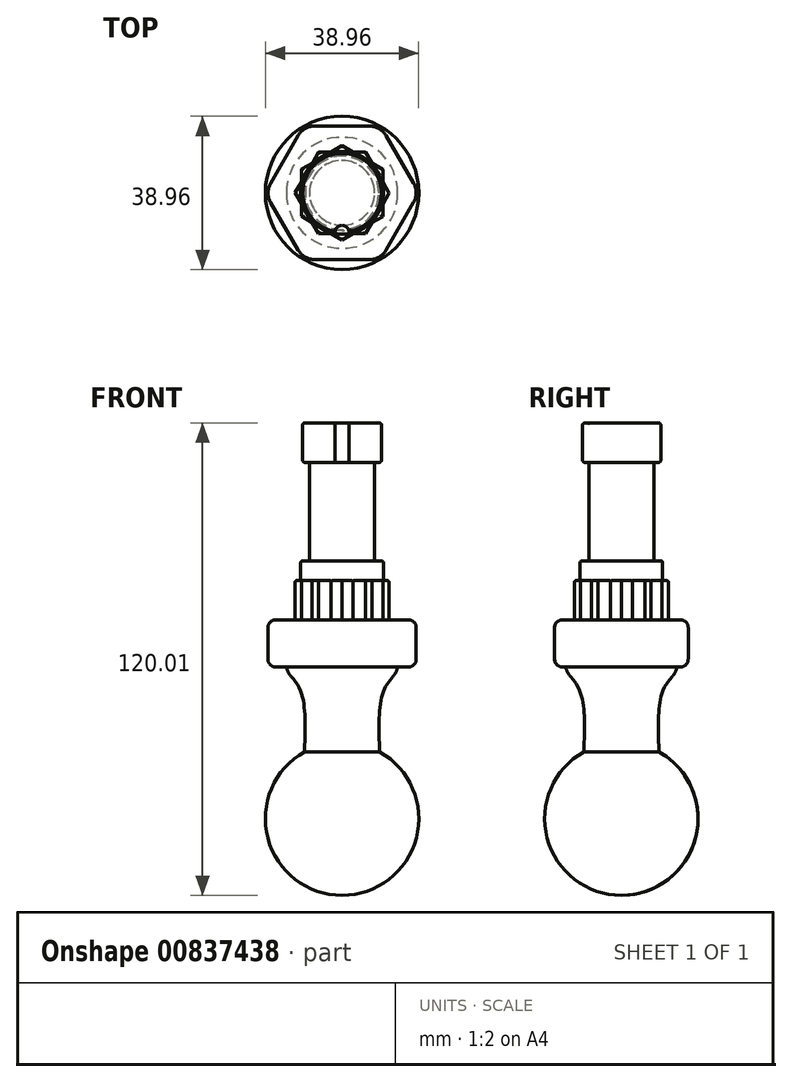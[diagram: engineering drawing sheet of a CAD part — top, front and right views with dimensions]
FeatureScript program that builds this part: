
annotation { "Feature Type Name" : "Feature", "Feature Type Description" : "" }
export const myFeature = defineFeature(function(context is Context, id is Id, definition is map)
    precondition{}
    {
        {
            var Q0;
            Q0=qCreatedBy(makeId("Top.planeOp"),FACE);
            var sketch = newSketch(context, id + "F0", { "sketchPlane" : qUnion([Q0])});
            skCircle(sketch, "E0.cCircle", {"center": v(0, 0) * mm, "radius": 11.95 * mm, "construction": true});
            skLineSegment(sketch, "E0.0", {"start": v(10.36, 5.96) * mm, "end": v(10.36, 2.75) * mm});
            skLineSegment(sketch, "E0.1", {"start": v(10.34, -6) * mm, "end": v(7.56, -7.6) * mm});
            skLineSegment(sketch, "E0.2", {"start": v(-0.02, -11.95) * mm, "end": v(-2.8, -10.34) * mm});
            skLineSegment(sketch, "E0.3", {"start": v(-10.36, -5.96) * mm, "end": v(-10.36, -2.75) * mm});
            skLineSegment(sketch, "E0.4", {"start": v(-10.34, 6) * mm, "end": v(-7.56, 7.6) * mm});
            skLineSegment(sketch, "E0.5", {"start": v(0.02, 11.95) * mm, "end": v(2.8, 10.34) * mm});
            skLineSegment(sketch, "E1", {"start": v(6, 10.34) * mm, "end": v(6.72, 11.59) * mm, "construction": true});
            skLineSegment(sketch, "E2.0", {"start": v(6, 10.34) * mm, "end": v(7.6, 7.56) * mm});
            skLineSegment(sketch, "E2.1", {"start": v(11.95, -0.02) * mm, "end": v(10.34, -2.8) * mm});
            skLineSegment(sketch, "E2.2", {"start": v(5.96, -10.36) * mm, "end": v(2.75, -10.36) * mm});
            skLineSegment(sketch, "E2.3", {"start": v(-6, -10.34) * mm, "end": v(-7.6, -7.56) * mm});
            skLineSegment(sketch, "E2.4", {"start": v(-11.95, 0.02) * mm, "end": v(-10.34, 2.8) * mm});
            skLineSegment(sketch, "E2.5", {"start": v(-5.96, 10.36) * mm, "end": v(-2.75, 10.36) * mm});
            skLineSegment(sketch, "E3.trimOffspring", {"start": v(-7.6, -7.56) * mm, "end": v(-10.36, -5.96) * mm});
            skPoint(sketch, "E4.orphan", {"position": v(-5.2, -8.95) * mm});
            skLineSegment(sketch, "E5.trimOffspring", {"start": v(-10.36, -2.75) * mm, "end": v(-11.95, 0.02) * mm});
            skLineSegment(sketch, "E6.trimOffspring", {"start": v(-2.8, -10.34) * mm, "end": v(-6, -10.34) * mm});
            skLineSegment(sketch, "E7.trimOffspring", {"start": v(2.75, -10.36) * mm, "end": v(-0.02, -11.95) * mm});
            skLineSegment(sketch, "E8.trimOffspring", {"start": v(7.56, -7.6) * mm, "end": v(5.96, -10.36) * mm});
            skLineSegment(sketch, "E9.trimOffspring", {"start": v(-10.34, 2.8) * mm, "end": v(-10.34, 6) * mm});
            skLineSegment(sketch, "E10.trimOffspring", {"start": v(-7.56, 7.6) * mm, "end": v(-5.96, 10.36) * mm});
            skLineSegment(sketch, "E11.trimOffspring", {"start": v(-2.75, 10.36) * mm, "end": v(0.02, 11.95) * mm});
            skLineSegment(sketch, "E12.trimOffspring", {"start": v(2.8, 10.34) * mm, "end": v(6, 10.34) * mm});
            skLineSegment(sketch, "E13.trimOffspring", {"start": v(7.6, 7.56) * mm, "end": v(10.36, 5.96) * mm});
            skPoint(sketch, "E14.orphan", {"position": v(5.2, 8.95) * mm});
            skLineSegment(sketch, "E15.trimOffspring", {"start": v(10.36, 2.75) * mm, "end": v(11.95, -0.02) * mm});
            skLineSegment(sketch, "E16.trimOffspring", {"start": v(10.34, -2.8) * mm, "end": v(10.34, -6) * mm});
            skSolve(sketch);
        }
        {
            var Q0;
            Q0=makeQuery(id+"F0.imprint","IMPRINT",FACE,{"disambiguationData":[TD([[makeQuery(id+"F0.imprint","IMPRINT",EDGE,{"derivedFrom":sQuery(id+"F0.wireOp",EDGE,"E0.0")}),-1.0]])]});
            extrude(context, id + "F1", {"entities" : qUnion([Q0]), "depth" : 10 * mm, "offsetDistance" : 25 * mm});
        }
        {
            var Q0;
            Q0=makeQuery(id+"F1.opExtrude","CAP_FACE",FACE,{"disambiguationData":[OSD([sQuery(id+"F0.wireOp",EDGE,"E0.0"),sQuery(id+"F0.wireOp",EDGE,"E0.1"),sQuery(id+"F0.wireOp",EDGE,"E0.2"),sQuery(id+"F0.wireOp",EDGE,"E0.3"),sQuery(id+"F0.wireOp",EDGE,"E0.4"),sQuery(id+"F0.wireOp",EDGE,"E0.5"),sQuery(id+"F0.wireOp",EDGE,"E2.0"),sQuery(id+"F0.wireOp",EDGE,"E2.1"),sQuery(id+"F0.wireOp",EDGE,"E2.2"),sQuery(id+"F0.wireOp",EDGE,"E2.3"),sQuery(id+"F0.wireOp",EDGE,"E2.4"),sQuery(id+"F0.wireOp",EDGE,"E2.5"),sQuery(id+"F0.wireOp",EDGE,"E3.trimOffspring"),sQuery(id+"F0.wireOp",EDGE,"E5.trimOffspring"),sQuery(id+"F0.wireOp",EDGE,"E6.trimOffspring"),sQuery(id+"F0.wireOp",EDGE,"E7.trimOffspring"),sQuery(id+"F0.wireOp",EDGE,"E8.trimOffspring"),sQuery(id+"F0.wireOp",EDGE,"E9.trimOffspring"),sQuery(id+"F0.wireOp",EDGE,"E10.trimOffspring"),sQuery(id+"F0.wireOp",EDGE,"E11.trimOffspring"),sQuery(id+"F0.wireOp",EDGE,"E12.trimOffspring"),sQuery(id+"F0.wireOp",EDGE,"E13.trimOffspring"),sQuery(id+"F0.wireOp",EDGE,"E15.trimOffspring"),sQuery(id+"F0.wireOp",EDGE,"E16.trimOffspring")])],"isStart":false});
            var sketch = newSketch(context, id + "F2", { "sketchPlane" : qUnion([Q0])});
            skLineSegment(sketch, "E17", {"start": v(-10.36, -2.75) * mm, "end": v(10.36, 2.75) * mm, "construction": true});
            skLineSegment(sketch, "E18", {"start": v(2.75, -10.36) * mm, "end": v(-2.75, 10.36) * mm, "construction": true});
            skCircle(sketch, "E19", {"center": v(0, 0) * mm, "radius": 10.5 * mm});
            skSolve(sketch);
        }
        {
            var Q0;
            Q0=makeQuery(id+"F2.imprint","IMPRINT",FACE,{"disambiguationData":[TD([[makeQuery(id+"F2.imprint","IMPRINT",EDGE,{"derivedFrom":sQuery(id+"F2.wireOp",EDGE,"E19")}),1.0]])]});
            extrude(context, id + "F3", {"entities" : qUnion([Q0]), "operationType" : NewBodyOperationType.ADD, "depth" : 5 * mm, "offsetDistance" : 25 * mm});
        }
        {
            var Q0;
            Q0=makeQuery(id+"F1.opExtrude","CAP_EDGE",EDGE,{"disambiguationData":[OSD([sQuery(id+"F0.wireOp",EDGE,"E2.5")])],"isStart":false});
            var Q1;
            Q1=makeQuery(id+"F1.opExtrude","CAP_EDGE",EDGE,{"disambiguationData":[OSD([sQuery(id+"F0.wireOp",EDGE,"E10.trimOffspring")])],"isStart":false});
            var Q2;
            Q2=makeQuery(id+"F1.opExtrude","CAP_EDGE",EDGE,{"disambiguationData":[OSD([sQuery(id+"F0.wireOp",EDGE,"E0.4")])],"isStart":false});
            var Q3;
            Q3=makeQuery(id+"F1.opExtrude","CAP_EDGE",EDGE,{"disambiguationData":[OSD([sQuery(id+"F0.wireOp",EDGE,"E9.trimOffspring")])],"isStart":false});
            var Q4;
            Q4=makeQuery(id+"F1.opExtrude","CAP_EDGE",EDGE,{"disambiguationData":[OSD([sQuery(id+"F0.wireOp",EDGE,"E2.4")])],"isStart":false});
            var Q5;
            Q5=makeQuery(id+"F1.opExtrude","CAP_EDGE",EDGE,{"disambiguationData":[OSD([sQuery(id+"F0.wireOp",EDGE,"E5.trimOffspring")])],"isStart":false});
            var Q6;
            Q6=makeQuery(id+"F1.opExtrude","CAP_EDGE",EDGE,{"disambiguationData":[OSD([sQuery(id+"F0.wireOp",EDGE,"E0.3")])],"isStart":false});
            var Q7;
            Q7=makeQuery(id+"F1.opExtrude","CAP_EDGE",EDGE,{"disambiguationData":[OSD([sQuery(id+"F0.wireOp",EDGE,"E3.trimOffspring")])],"isStart":false});
            var Q8;
            Q8=makeQuery(id+"F1.opExtrude","CAP_EDGE",EDGE,{"disambiguationData":[OSD([sQuery(id+"F0.wireOp",EDGE,"E2.3")])],"isStart":false});
            var Q9;
            Q9=makeQuery(id+"F1.opExtrude","CAP_EDGE",EDGE,{"disambiguationData":[OSD([sQuery(id+"F0.wireOp",EDGE,"E6.trimOffspring")])],"isStart":false});
            var Q10;
            Q10=makeQuery(id+"F1.opExtrude","CAP_EDGE",EDGE,{"disambiguationData":[OSD([sQuery(id+"F0.wireOp",EDGE,"E0.2")])],"isStart":false});
            var Q11;
            Q11=makeQuery(id+"F1.opExtrude","CAP_EDGE",EDGE,{"disambiguationData":[OSD([sQuery(id+"F0.wireOp",EDGE,"E7.trimOffspring")])],"isStart":false});
            var Q12;
            Q12=makeQuery(id+"F1.opExtrude","CAP_EDGE",EDGE,{"disambiguationData":[OSD([sQuery(id+"F0.wireOp",EDGE,"E2.2")])],"isStart":false});
            var Q13;
            Q13=makeQuery(id+"F1.opExtrude","CAP_EDGE",EDGE,{"disambiguationData":[OSD([sQuery(id+"F0.wireOp",EDGE,"E8.trimOffspring")])],"isStart":false});
            var Q14;
            Q14=makeQuery(id+"F1.opExtrude","CAP_EDGE",EDGE,{"disambiguationData":[OSD([sQuery(id+"F0.wireOp",EDGE,"E0.1")])],"isStart":false});
            var Q15;
            Q15=makeQuery(id+"F1.opExtrude","CAP_EDGE",EDGE,{"disambiguationData":[OSD([sQuery(id+"F0.wireOp",EDGE,"E16.trimOffspring")])],"isStart":false});
            var Q16;
            Q16=makeQuery(id+"F1.opExtrude","CAP_EDGE",EDGE,{"disambiguationData":[OSD([sQuery(id+"F0.wireOp",EDGE,"E2.1")])],"isStart":false});
            var Q17;
            Q17=makeQuery(id+"F1.opExtrude","CAP_EDGE",EDGE,{"disambiguationData":[OSD([sQuery(id+"F0.wireOp",EDGE,"E15.trimOffspring")])],"isStart":false});
            var Q18;
            Q18=makeQuery(id+"F1.opExtrude","CAP_EDGE",EDGE,{"disambiguationData":[OSD([sQuery(id+"F0.wireOp",EDGE,"E0.0")])],"isStart":false});
            var Q19;
            Q19=makeQuery(id+"F1.opExtrude","CAP_EDGE",EDGE,{"disambiguationData":[OSD([sQuery(id+"F0.wireOp",EDGE,"E13.trimOffspring")])],"isStart":false});
            var Q20;
            Q20=makeQuery(id+"F1.opExtrude","CAP_EDGE",EDGE,{"disambiguationData":[OSD([sQuery(id+"F0.wireOp",EDGE,"E2.0")])],"isStart":false});
            var Q21;
            Q21=makeQuery(id+"F1.opExtrude","CAP_EDGE",EDGE,{"disambiguationData":[OSD([sQuery(id+"F0.wireOp",EDGE,"E12.trimOffspring")])],"isStart":false});
            var Q22;
            Q22=makeQuery(id+"F1.opExtrude","CAP_EDGE",EDGE,{"disambiguationData":[OSD([sQuery(id+"F0.wireOp",EDGE,"E0.5")])],"isStart":false});
            var Q23;
            Q23=makeQuery(id+"F1.opExtrude","CAP_EDGE",EDGE,{"disambiguationData":[OSD([sQuery(id+"F0.wireOp",EDGE,"E11.trimOffspring")])],"isStart":false});
            fillet(context, id + "F4", {"entities" : qUnion([Q0, Q1, Q2, Q3, Q4, Q5, Q6, Q7, Q8, Q9, Q10, Q11, Q12, Q13, Q14, Q15, Q16, Q17, Q18, Q19, Q20, Q21, Q22, Q23]), "radius" : .5 * mm, "tangentPropagation" : true, "allowEdgeOverflow" : false});
        }
        {
            var Q0;
            Q0=makeQuery(id+"F3.opExtrude","CAP_FACE",FACE,{"disambiguationData":[OSD([sQuery(id+"F2.wireOp",EDGE,"E19")])],"isStart":false});
            var sketch = newSketch(context, id + "F5", { "sketchPlane" : qUnion([Q0])});
            skCircle(sketch, "E20", {"center": v(0, 0) * mm, "radius": 8.25 * mm});
            skSolve(sketch);
        }
        {
            var Q0;
            Q0=makeQuery(id+"F5.imprint","IMPRINT",FACE,{"disambiguationData":[TD([[makeQuery(id+"F5.imprint","IMPRINT",EDGE,{"derivedFrom":sQuery(id+"F5.wireOp",EDGE,"E20")}),1.0]])]});
            extrude(context, id + "F6", {"entities" : qUnion([Q0]), "operationType" : NewBodyOperationType.ADD, "depth" : 25 * mm, "offsetDistance" : 25 * mm});
        }
        {
            var Q0;
            Q0=makeQuery(id+"F6.opExtrude","CAP_FACE",FACE,{"disambiguationData":[OSD([sQuery(id+"F5.wireOp",EDGE,"E20")])],"isStart":false});
            var sketch = newSketch(context, id + "F7", { "sketchPlane" : qUnion([Q0])});
            skCircle(sketch, "E21", {"center": v(0, 0) * mm, "radius": 10 * mm});
            skSolve(sketch);
        }
        {
            var Q0;
            Q0=makeQuery(id+"F7.imprint","IMPRINT",FACE,{"disambiguationData":[TD([[makeQuery(id+"F7.imprint","IMPRINT",EDGE,{"derivedFrom":sQuery(id+"F7.wireOp",EDGE,"E21")}),1.0]])]});
            var Q1;
            Q1=makeQuery(id+"F7.imprint","IMPRINT",FACE,{"disambiguationData":[TD([[makeQuery(id+"F7.imprint","IMPRINT",EDGE,{"derivedFrom":makeQuery(id+"F6.opExtrude","CAP_EDGE",EDGE,{"disambiguationData":[OSD([sQuery(id+"F5.wireOp",EDGE,"E20")])],"isStart":false})}),1.0]])]});
            extrude(context, id + "F8", {"entities" : qUnion([Q0, Q1]), "operationType" : NewBodyOperationType.ADD, "depth" : 10 * mm, "offsetDistance" : 25 * mm});
        }
        {
            var Q0;
            Q0=makeQuery(id+"F8.opExtrude","CAP_FACE",FACE,{"disambiguationData":[OSD([sQuery(id+"F7.wireOp",EDGE,"E21")])],"isStart":true});
            var sketch = newSketch(context, id + "F9", { "sketchPlane" : qUnion([Q0])});
            skLineSegment(sketch, "E22", {"start": v(0, 10) * mm, "end": v(0, 8.25) * mm, "construction": true});
            skArc(sketch, "E23", {"start": v(0, 8.25) * mm, "mid": v(1.18, 8.7) * mm, "end": v(1.74, 9.85) * mm});
            skArc(sketch, "E24", {"start": v(0, 8.25) * mm, "mid": v(-1.18, 8.7) * mm, "end": v(-1.74, 9.85) * mm});
            skSolve(sketch);
        }
        {
            var Q0;
            {var subQ0=sQuery(id+"F9.wireOp",EDGE,"E23");Q0=makeQuery(id+"F9.imprint","IMPRINT",FACE,{"disambiguationData":[TD([[makeQuery(id+"F9.imprint","IMPRINT",EDGE,{"derivedFrom":subQ0}),1.0]])]});}
            extrude(context, id + "F10", {"entities" : qUnion([Q0]), "operationType" : NewBodyOperationType.REMOVE, "oppositeDirection" : true, "depth" : 25 * mm, "offsetDistance" : 25 * mm});
        }
        {
            var Q0;
            Q0=makeQuery(id+"F8.opExtrude","CAP_EDGE",EDGE,{"disambiguationData":[OSD([sQuery(id+"F7.wireOp",EDGE,"E21")])],"isStart":false});
            var Q1;
            Q1=makeQuery(id+"F10.boolean.opBoolean","INTERSECT",EDGE,{"derivedFrom":[makeQuery(id+"F8.opExtrude","CAP_FACE",FACE,{"disambiguationData":[OSD([sQuery(id+"F7.wireOp",EDGE,"E21")])],"isStart":false}),makeQuery(id+"F10.opExtrude","SWEPT_FACE",FACE,{"disambiguationData":[OSD([sQuery(id+"F9.wireOp",EDGE,"E23"),sQuery(id+"F9.wireOp",EDGE,"E24")])]})]});
            var Q2;
            Q2=makeQuery(id+"F10.boolean.opBoolean","COPY",EDGE,{"derivedFrom":makeQuery(id+"F10.opExtrude","SWEPT_EDGE",EDGE,{"disambiguationData":[OSD([sQuery(id+"F7.wireOp",EDGE,"E21"),sQuery(id+"F9.wireOp",EDGE,"E24")])]})});
            var Q3;
            Q3=makeQuery(id+"F10.boolean.opBoolean","COPY",EDGE,{"derivedFrom":makeQuery(id+"F10.opExtrude","SWEPT_EDGE",EDGE,{"disambiguationData":[OSD([sQuery(id+"F7.wireOp",EDGE,"E21"),sQuery(id+"F9.wireOp",EDGE,"E23")])]})});
            var Q4;
            Q4=makeQuery(id+"F8.opExtrude","CAP_EDGE",EDGE,{"disambiguationData":[OSD([sQuery(id+"F7.wireOp",EDGE,"E21")])],"isStart":true});
            var Q5;
            Q5=makeQuery(id+"F10.boolean.opBoolean","COPY",EDGE,{"disambiguationData":[OD(1.0)],"derivedFrom":makeQuery(id+"F10.opExtrude","CAP_EDGE",EDGE,{"disambiguationData":[OSD([sQuery(id+"F9.wireOp",EDGE,"E23"),sQuery(id+"F9.wireOp",EDGE,"E24")])],"isStart":true})});
            var Q6;
            Q6=makeQuery(id+"F10.boolean.opBoolean","COPY",EDGE,{"disambiguationData":[OD(0.0)],"derivedFrom":makeQuery(id+"F10.opExtrude","CAP_EDGE",EDGE,{"disambiguationData":[OSD([sQuery(id+"F9.wireOp",EDGE,"E23"),sQuery(id+"F9.wireOp",EDGE,"E24")])],"isStart":true})});
            fillet(context, id + "F11", {"entities" : qUnion([Q0, Q1, Q2, Q3, Q4, Q5, Q6]), "radius" : .5 * mm, "tangentPropagation" : true, "allowEdgeOverflow" : false});
        }
        {
            var Q0;
            Q0=makeQuery(id+"F6.opExtrude","CAP_EDGE",EDGE,{"disambiguationData":[OSD([sQuery(id+"F5.wireOp",EDGE,"E20")])],"isStart":true});
            var Q1;
            Q1=makeQuery(id+"F3.opExtrude","CAP_EDGE",EDGE,{"disambiguationData":[OSD([sQuery(id+"F2.wireOp",EDGE,"E19")])],"isStart":false});
            fillet(context, id + "F12", {"entities" : qUnion([Q0, Q1]), "radius" : .5 * mm, "tangentPropagation" : true, "allowEdgeOverflow" : false});
        }
        {
            var Q0;
            Q0=makeQuery(id+"F1.opExtrude","CAP_FACE",FACE,{"disambiguationData":[OSD([sQuery(id+"F0.wireOp",EDGE,"E0.0"),sQuery(id+"F0.wireOp",EDGE,"E0.1"),sQuery(id+"F0.wireOp",EDGE,"E0.2"),sQuery(id+"F0.wireOp",EDGE,"E0.3"),sQuery(id+"F0.wireOp",EDGE,"E0.4"),sQuery(id+"F0.wireOp",EDGE,"E0.5"),sQuery(id+"F0.wireOp",EDGE,"E2.0"),sQuery(id+"F0.wireOp",EDGE,"E2.1"),sQuery(id+"F0.wireOp",EDGE,"E2.2"),sQuery(id+"F0.wireOp",EDGE,"E2.3"),sQuery(id+"F0.wireOp",EDGE,"E2.4"),sQuery(id+"F0.wireOp",EDGE,"E2.5"),sQuery(id+"F0.wireOp",EDGE,"E3.trimOffspring"),sQuery(id+"F0.wireOp",EDGE,"E5.trimOffspring"),sQuery(id+"F0.wireOp",EDGE,"E6.trimOffspring"),sQuery(id+"F0.wireOp",EDGE,"E7.trimOffspring"),sQuery(id+"F0.wireOp",EDGE,"E8.trimOffspring"),sQuery(id+"F0.wireOp",EDGE,"E9.trimOffspring"),sQuery(id+"F0.wireOp",EDGE,"E10.trimOffspring"),sQuery(id+"F0.wireOp",EDGE,"E11.trimOffspring"),sQuery(id+"F0.wireOp",EDGE,"E12.trimOffspring"),sQuery(id+"F0.wireOp",EDGE,"E13.trimOffspring"),sQuery(id+"F0.wireOp",EDGE,"E15.trimOffspring"),sQuery(id+"F0.wireOp",EDGE,"E16.trimOffspring")])],"isStart":true});
            var sketch = newSketch(context, id + "F13", { "sketchPlane" : qUnion([Q0])});
            skCircle(sketch, "E25.cCircle", {"center": v(0, 0) * mm, "radius": 16.96 * mm, "construction": true});
            skLineSegment(sketch, "E25.0", {"start": v(-11.22, -14.53) * mm, "end": v(-18.17, -2.4) * mm});
            skLineSegment(sketch, "E25.1", {"start": v(-18.16, 2.5) * mm, "end": v(-11.17, 14.54) * mm});
            skLineSegment(sketch, "E25.2", {"start": v(-6.92, 16.98) * mm, "end": v(7.06, 16.94) * mm});
            skLineSegment(sketch, "E25.3", {"start": v(11.22, 14.53) * mm, "end": v(18.2, 2.35) * mm});
            skLineSegment(sketch, "E25.4", {"start": v(18.2, -2.45) * mm, "end": v(11.17, -14.54) * mm});
            skLineSegment(sketch, "E25.5", {"start": v(6.92, -16.98) * mm, "end": v(-7.06, -16.94) * mm});
            skPoint(sketch, "E25.0.midPoint", {"position": v(-14.7, -8.44) * mm});
            skPoint(sketch, "E26.visualSharp", {"position": v(9.75, -16.99) * mm});
            skArc(sketch, "E26.filletArc", {"start": v(6.92, -16.98) * mm, "mid": v(9.37, -16.33) * mm, "end": v(11.17, -14.54) * mm});
            skPoint(sketch, "E27.visualSharp", {"position": v(-9.84, -16.93) * mm});
            skArc(sketch, "E27.filletArc", {"start": v(-11.22, -14.53) * mm, "mid": v(-9.46, -16.3) * mm, "end": v(-7.06, -16.94) * mm});
            skPoint(sketch, "E28.visualSharp", {"position": v(-19.58, 0.05) * mm});
            skArc(sketch, "E28.filletArc", {"start": v(-18.16, 2.5) * mm, "mid": v(-18.82, 0.05) * mm, "end": v(-18.17, -2.4) * mm});
            skPoint(sketch, "E29.visualSharp", {"position": v(-9.75, 16.99) * mm});
            skArc(sketch, "E29.filletArc", {"start": v(-6.92, 16.98) * mm, "mid": v(-9.37, 16.33) * mm, "end": v(-11.17, 14.54) * mm});
            skPoint(sketch, "E30.visualSharp", {"position": v(9.84, 16.93) * mm});
            skArc(sketch, "E30.filletArc", {"start": v(11.22, 14.53) * mm, "mid": v(9.46, 16.3) * mm, "end": v(7.06, 16.94) * mm});
            skPoint(sketch, "E31.visualSharp", {"position": v(19.58, -0.05) * mm});
            skArc(sketch, "E31.filletArc", {"start": v(18.2, -2.45) * mm, "mid": v(18.84, -0.05) * mm, "end": v(18.2, 2.35) * mm});
            skSolve(sketch);
        }
        {
            var Q0;
            Q0=makeQuery(id+"F13.imprint","IMPRINT",FACE,{"disambiguationData":[TD([[makeQuery(id+"F13.imprint","IMPRINT",EDGE,{"derivedFrom":sQuery(id+"F13.wireOp",EDGE,"XwkZxwQT-tXsu-qyU6-IrZG-78iqKTn2pKXx")}),1.0]])]});
            var Q1;
            Q1=makeQuery(id+"F13.imprint","IMPRINT",FACE,{"disambiguationData":[TD([[makeQuery(id+"F13.imprint","IMPRINT",EDGE,{"derivedFrom":makeQuery(id+"F1.opExtrude","CAP_EDGE",EDGE,{"disambiguationData":[OSD([sQuery(id+"F0.wireOp",EDGE,"E0.0")])],"isStart":true})}),1.0]])]});
            var Q2;
            Q2=makeQuery(id+"F13.imprint","IMPRINT",FACE,{"disambiguationData":[TD([[makeQuery(id+"F13.imprint","IMPRINT",EDGE,{"derivedFrom":sQuery(id+"F13.wireOp",EDGE,"E25.0")}),-1.0]])]});
            extrude(context, id + "F14", {"entities" : qUnion([Q0, Q1, Q2]), "operationType" : NewBodyOperationType.ADD, "depth" : 12 * mm, "offsetDistance" : 25 * mm});
        }
        {
            var Q0;
            Q0=makeQuery(id+"F14.opExtrude","CAP_EDGE",EDGE,{"disambiguationData":[OSD([sQuery(id+"F13.wireOp",EDGE,"XwkZxwQT-tXsu-qyU6-IrZG-78iqKTn2pKXx")])],"isStart":false});
            var Q1;
            Q1=makeQuery(id+"F14.opExtrude","CAP_EDGE",EDGE,{"disambiguationData":[OSD([sQuery(id+"F13.wireOp",EDGE,"XwkZxwQT-tXsu-qyU6-IrZG-78iqKTn2pKXx")])],"isStart":true});
            var Q2;
            Q2=makeQuery(id+"F14.opExtrude","CAP_EDGE",EDGE,{"disambiguationData":[OSD([sQuery(id+"F13.wireOp",EDGE,"E25.3")])],"isStart":false});
            var Q3;
            Q3=makeQuery(id+"F14.opExtrude","CAP_EDGE",EDGE,{"disambiguationData":[OSD([sQuery(id+"F13.wireOp",EDGE,"E25.3")])],"isStart":true});
            fillet(context, id + "F15", {"entities" : qUnion([Q0, Q1, Q2, Q3]), "radius" : 2 * mm, "tangentPropagation" : true, "allowEdgeOverflow" : false});
        }
        {
            var Q0;
            Q0=qCreatedBy(makeId("Right.planeOp"),FACE);
            var sketch = newSketch(context, id + "F16", { "sketchPlane" : qUnion([Q0])});
            skLineSegment(sketch, "E32", {"start": v(0, 0) * mm, "end": v(0, -58.93) * mm});
            skPoint(sketch, "E33.orphan", {"position": v(0, -54.24) * mm});
            skPoint(sketch, "E34.end.orphan", {"position": v(0, -52.5) * mm});
            skArc(sketch, "E35", {"start": v(13.72, -64.36) * mm, "mid": v(19.3, -47.92) * mm, "end": v(9.56, -33.55) * mm});
            skLineSegment(sketch, "E36", {"start": v(0, -12.6) * mm, "end": v(0, -64.36) * mm});
            skLineSegment(sketch, "E37", {"start": v(0, -11.95) * mm, "end": v(14.13, -11.95) * mm});
            skPoint(sketch, "E38.1.internal.orphan", {"position": v(14.13, -15.04) * mm});
            skPoint(sketch, "E39.orphan", {"position": v(14.13, -12.6) * mm});
            skLineSegment(sketch, "E40", {"start": v(14.13, -11.95) * mm, "end": v(14.13, -13.15) * mm});
            skFitSpline(sketch, "E41", {"points": [v(14.13, -13.15) * mm, v(10.35, -18.6) * mm, v(9.56, -33.55) * mm], "startDerivative": vector(-11.08, -11.39) * mm, "endDerivative": vector(1.12, -28.29) * mm});
            skArc(sketch, "E42", {"start": v(0, -70.01) * mm, "mid": v(18.85, -55.47) * mm, "end": v(9.56, -33.55) * mm});
            skLineSegment(sketch, "E43", {"start": v(0, -39.75) * mm, "end": v(0, -70.01) * mm});
            skSolve(sketch);
        }
        {
            var Q0;
            {var subQ1=sQuery(id+"F16.wireOp",EDGE,"NLwjia8V-UTQ4-TUgC-SJFi-TH08i8K1N5aU");Q0=makeQuery(id+"F16.imprint","IMPRINT",FACE,{"disambiguationData":[TD([[makeQuery(id+"F16.imprint","IMPRINT",EDGE,{"derivedFrom":subQ1}),-1.0]])]});}
            var Q1;
            Q1=makeQuery(id+"F16.imprint","IMPRINT",FACE,{"disambiguationData":[TD([[makeQuery(id+"F16.imprint","IMPRINT",EDGE,{"derivedFrom":sQuery(id+"F16.wireOp",EDGE,"E35")}),1.0]])]});
            var Q2;
            {var subQ0=sQuery(id+"F16.wireOp",EDGE,"E43");var subQ1=sQuery(id+"F16.wireOp",EDGE,"E36");var subQ2=makeQuery(id+"F16.imprint","INTERSECT",VERTEX,{"derivedFrom":[subQ1,subQ0]});Q2=makeQuery(id+"F16.imprint","IMPRINT",FACE,{"disambiguationData":[TD([[makeQuery(id+"F16.imprint","IMPRINT",EDGE,{"disambiguationData":[TD([[subQ2,1.0]])],"derivedFrom":subQ1}),1.0]])]});}
            var Q3;
            Q3=sQuery(id+"F16.wireOp",EDGE,"E32");
            revolve(context, id + "F17", {"operationType" : NewBodyOperationType.ADD, "surfaceOperationType" : NewSurfaceOperationType.NEW, "entities" : qUnion([Q0, Q1, Q2]), "axis" : qUnion([Q3]), "revolveType" : RevolveType.FULL});
        }
        {
            var Q0;
            Q0=makeQuery(id+"F17.opRevolve","SWEPT_EDGE",EDGE,{"disambiguationData":[OSD([sQuery(id+"F16.wireOp",EDGE,"E40"),sQuery(id+"F16.wireOp",EDGE,"E41")])]});
            fillet(context, id + "F18", {"entities" : qUnion([Q0]), "radius" : 5 * mm, "tangentPropagation" : true, "allowEdgeOverflow" : false});
        }
    });
